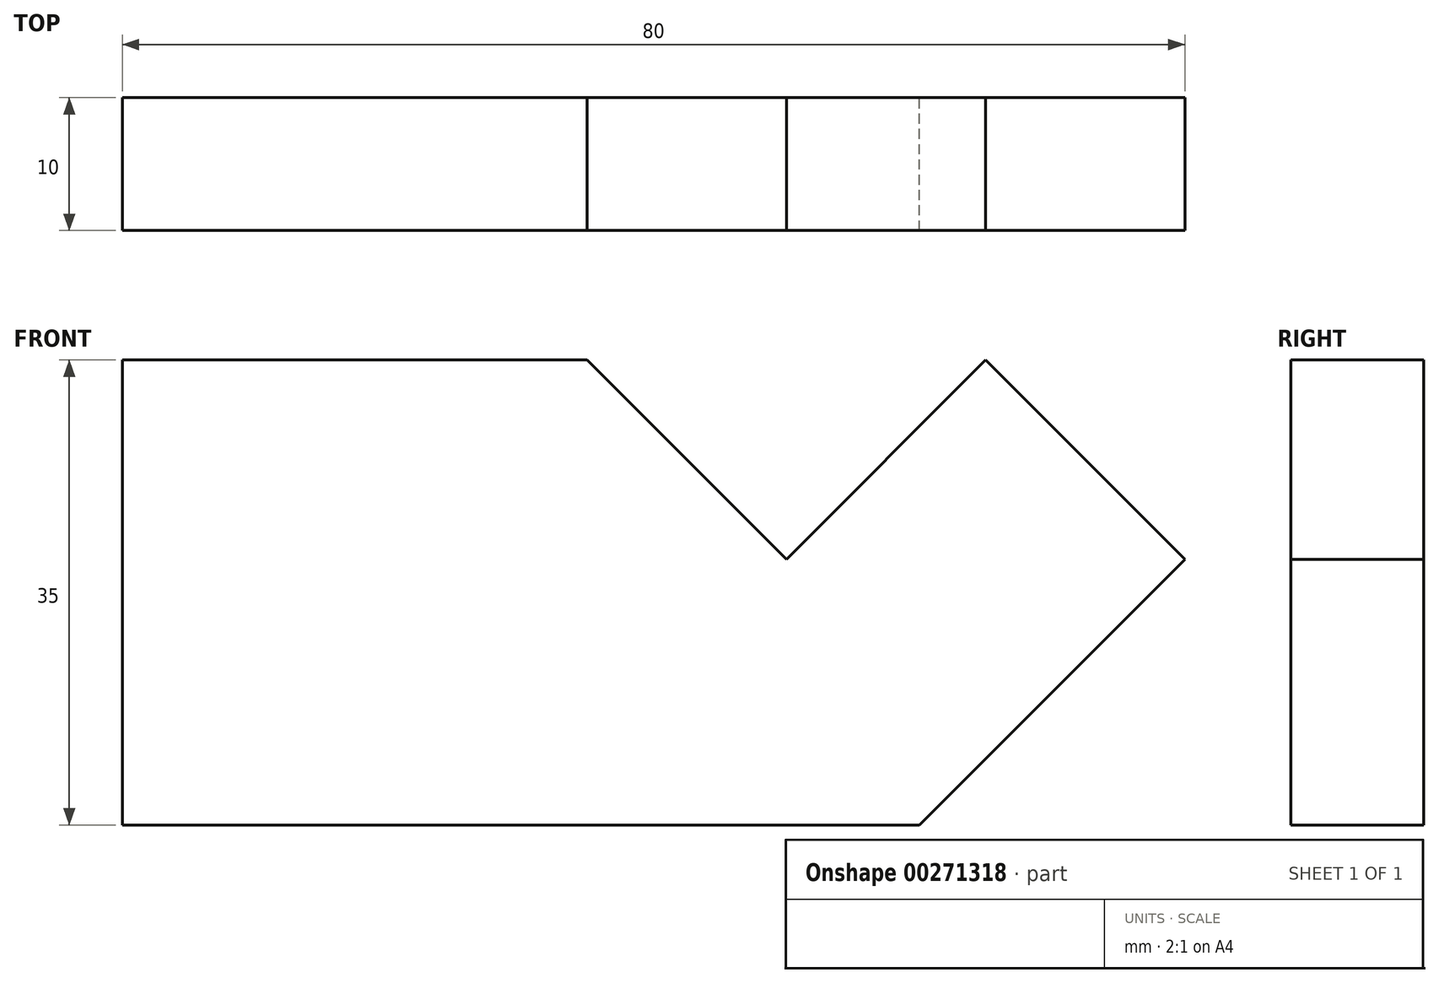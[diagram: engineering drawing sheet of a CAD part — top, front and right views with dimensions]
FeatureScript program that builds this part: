
annotation { "Feature Type Name" : "Feature", "Feature Type Description" : "" }
export const myFeature = defineFeature(function(context is Context, id is Id, definition is map)
    precondition{}
    {
        {
            var Q0;
            Q0=qCreatedBy(makeId("Front.planeOp"),FACE);
            var sketch = newSketch(context, id + "F0", { "sketchPlane" : qUnion([Q0])});
            skLineSegment(sketch, "E0", {"start": v(0, 0) * mm, "end": v(60, 0) * mm});
            skLineSegment(sketch, "E1", {"start": v(0, 0) * mm, "end": v(0, 35) * mm});
            skLineSegment(sketch, "E2", {"start": v(60, 0) * mm, "end": v(80, 20) * mm});
            skLineSegment(sketch, "E3", {"start": v(80, 20) * mm, "end": v(65, 35) * mm});
            skLineSegment(sketch, "E4", {"start": v(65, 35) * mm, "end": v(50, 20) * mm});
            skLineSegment(sketch, "E5", {"start": v(50, 20) * mm, "end": v(35, 35) * mm});
            skLineSegment(sketch, "E6", {"start": v(35, 35) * mm, "end": v(0, 35) * mm});
            skSolve(sketch);
        }
        {
            var Q0;
            Q0=makeQuery(id+"F0.imprint","IMPRINT",FACE,{"disambiguationData":[TD([[makeQuery(id+"F0.imprint","IMPRINT",EDGE,{"derivedFrom":sQuery(id+"F0.wireOp",EDGE,"E0")}),1.0]])]});
            extrude(context, id + "F1", {"entities" : qUnion([Q0]), "depth" : 10 * mm});
        }
    });
